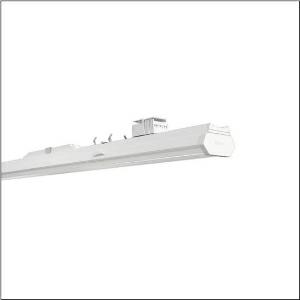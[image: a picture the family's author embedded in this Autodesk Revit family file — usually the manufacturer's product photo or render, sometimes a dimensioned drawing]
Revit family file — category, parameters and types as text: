
# Revit family: licross_r__21_performance_mo_52td16cn46xg_4d89
name_source: partatom
category: Lighting Fixtures
units: mm (PartAtom-declared; Revit-internal decimal feet)

## family parameters
Cut with Voids When Loaded = No
Host = Face
Light Source = No
Part Type = Normal
Room Calculation Point = No
Round Connector Dimension = Use Diameter
Shared = No

## types (1)
- --- (1 x LED, 6000 lm, 32 W, 4000K)
    Apparent Load = 32 VA
    CIE Flux Codes = 66 88 96 79 100
    Color Rendering = 80
    Color Temperature = 4000K
    Default Elevation = 1800 mm
    Description = Licross® 21 Performance MO, luminaire insert, of sheet steel, galvanised, coil coated, white, length: 1.500mm, width: 120mm, height: 123mm, LED rated luminous flux: 6.000lm, light colour: 840, control gear: ON/OFF Multilumen, CLOi, control gear: ECG Multilumen, with plug, 3-pole, with phase selection, mains connection: 220..240V, AC, 50/60Hz, halogen-free wiring, primary light control with lens, of plastic, primary optical cover: cover, of PMMA, light emission: direct/indirect distribution, primary light characteristic: symmetric, protection rating (complete): IP54, insulation class (complete): insulation class I (protective earthing), certification: CE, ENEC, UKCA, protection symbol: D if used in an environment with non-conductive dust loads with corresponding accessories, impact resistance: IK06, permissible ambient temperature for indoor applications: -35..+55°C, corresponds to IFS (International Featured Standards) requirements for safety and quality in the food industry, reducing of maximum allowable ambient temperature of 5°C with ceiling mounting, LABS conformity tested according to VDMA 24364:2018-05, packaging unit: 1 piece
    Height = 114 mm
    Lamp = 1 x LED
    Lamp Light Flux = 6000 lm
    Lamp Power = 32 W
    Lamp count = 1
    Length = 1500 mm
    Luminous efficacy = 188 lm/W
    Manufacturer = Siteco
    ModVariant = No
    Model = 52TD16CN46XG
    Mounting Place = Ceiling
    Mounting Type = Pendant
    Number of Poles = 1
    OnlyDefault = Yes
    Power Factor = 1
    Product Name = Licross® 21 Performance MO
    Product group = luminaire insert
    ProductGroupID = 902
    Protection Class = Protection class I
    Protection Degree = IP 54
    RLX_Detail_Level = 1
    RlxData = <blob elided: 29597 chars, md5=aa87fb5a>
    Socket = socket
    Standby Power = 0 W
    System Light Flux = 6000 lm
    System Power = 32 W
    Type Comments = factory setting: luminous flux: 100 % | (A | C | E) | 74 mA
    Type Image = l_1256148.jpg
    URL = http://relux.com
    VarID = @adj_019969
    Voltage = 0 V
    Weight = 0.00 kg
    Width = 120 mm

## geometry (parser evidence)
native form markers: Blend x4, Sweep x13
no freeform markers — native parametric forms only
